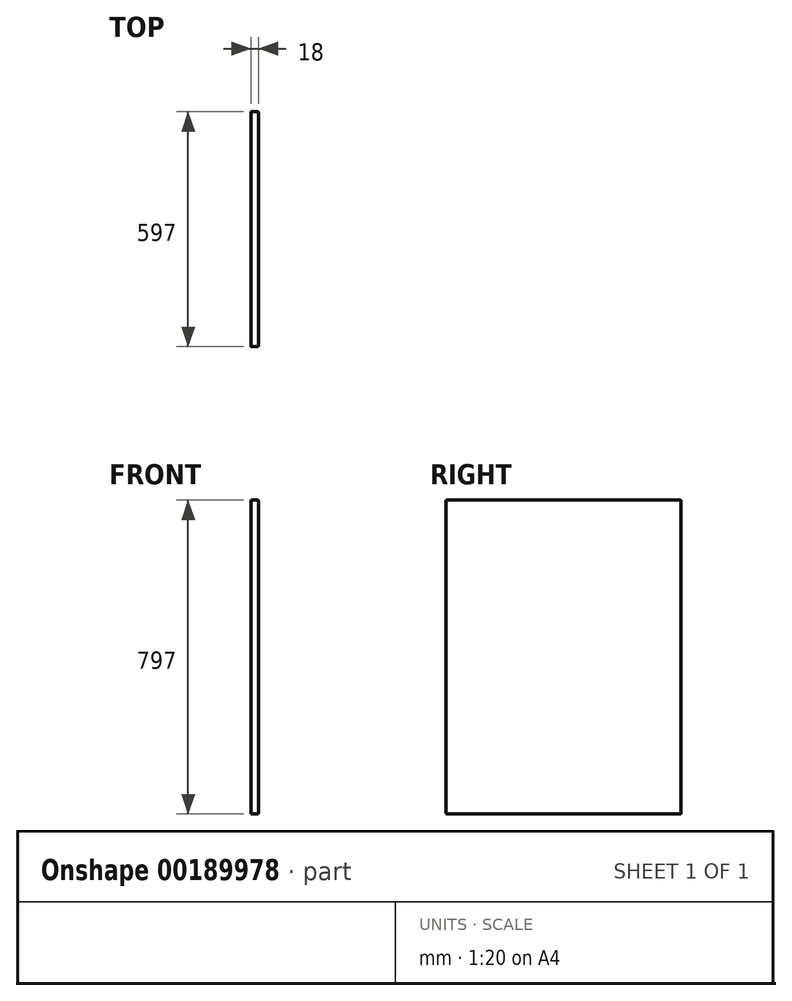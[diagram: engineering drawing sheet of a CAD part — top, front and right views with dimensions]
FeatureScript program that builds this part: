
annotation { "Feature Type Name" : "Feature", "Feature Type Description" : "" }
export const myFeature = defineFeature(function(context is Context, id is Id, definition is map)
    precondition{}
    {
        {
            var Q0;
            Q0=qCreatedBy(makeId("Right.planeOp"),FACE);
            var sketch = newSketch(context, id + "F0", { "sketchPlane" : qUnion([Q0])});
            skLineSegment(sketch, "E0.bottom", {"start": v(-285.92, -374.43) * mm, "end": v(311.08, -374.43) * mm});
            skLineSegment(sketch, "E0.top", {"start": v(-285.92, 422.57) * mm, "end": v(311.08, 422.57) * mm});
            skLineSegment(sketch, "E0.left", {"start": v(-285.92, -374.43) * mm, "end": v(-285.92, 422.57) * mm});
            skLineSegment(sketch, "E0.right", {"start": v(311.08, -374.43) * mm, "end": v(311.08, 422.57) * mm});
            skSolve(sketch);
        }
        {
            var Q0;
            Q0=makeQuery(id+"F0.imprint","IMPRINT",FACE,{"disambiguationData":[TD([[makeQuery(id+"F0.imprint","IMPRINT",EDGE,{"derivedFrom":sQuery(id+"F0.wireOp",EDGE,"E0.bottom")}),1.0]])]});
            extrude(context, id + "F1", {"entities" : qUnion([Q0]), "depth" : 18 * mm});
        }
        {
            var Q0;
            Q0=makeQuery(id+"F1.opExtrude","CAP_FACE",FACE,{"disambiguationData":[OSD([sQuery(id+"F0.wireOp",EDGE,"E0.bottom"),sQuery(id+"F0.wireOp",EDGE,"E0.top"),sQuery(id+"F0.wireOp",EDGE,"E0.left"),sQuery(id+"F0.wireOp",EDGE,"E0.right")])],"isStart":false});
            var Q1;
            Q1=makeQuery(id+"F1.opExtrude","SWEPT_EDGE",EDGE,{"disambiguationData":[OSD([sQuery(id+"F0.wireOp",EDGE,"E0.top"),sQuery(id+"F0.wireOp",EDGE,"E0.left")])]});
            var Q2;
            Q2=makeQuery(id+"F1.opExtrude","SWEPT_EDGE",EDGE,{"disambiguationData":[OSD([sQuery(id+"F0.wireOp",EDGE,"E0.top"),sQuery(id+"F0.wireOp",EDGE,"E0.right")])]});
            var Q3;
            Q3=makeQuery(id+"F1.opExtrude","SWEPT_EDGE",EDGE,{"disambiguationData":[OSD([sQuery(id+"F0.wireOp",EDGE,"E0.bottom"),sQuery(id+"F0.wireOp",EDGE,"E0.right")])]});
            var Q4;
            Q4=makeQuery(id+"F1.opExtrude","SWEPT_EDGE",EDGE,{"disambiguationData":[OSD([sQuery(id+"F0.wireOp",EDGE,"E0.bottom"),sQuery(id+"F0.wireOp",EDGE,"E0.left")])]});
            fillet(context, id + "F2", {"entities" : qUnion([Q0, Q1, Q2, Q3, Q4]), "radius" : 2 * mm, "tangentPropagation" : true, "allowEdgeOverflow" : false});
        }
    });
